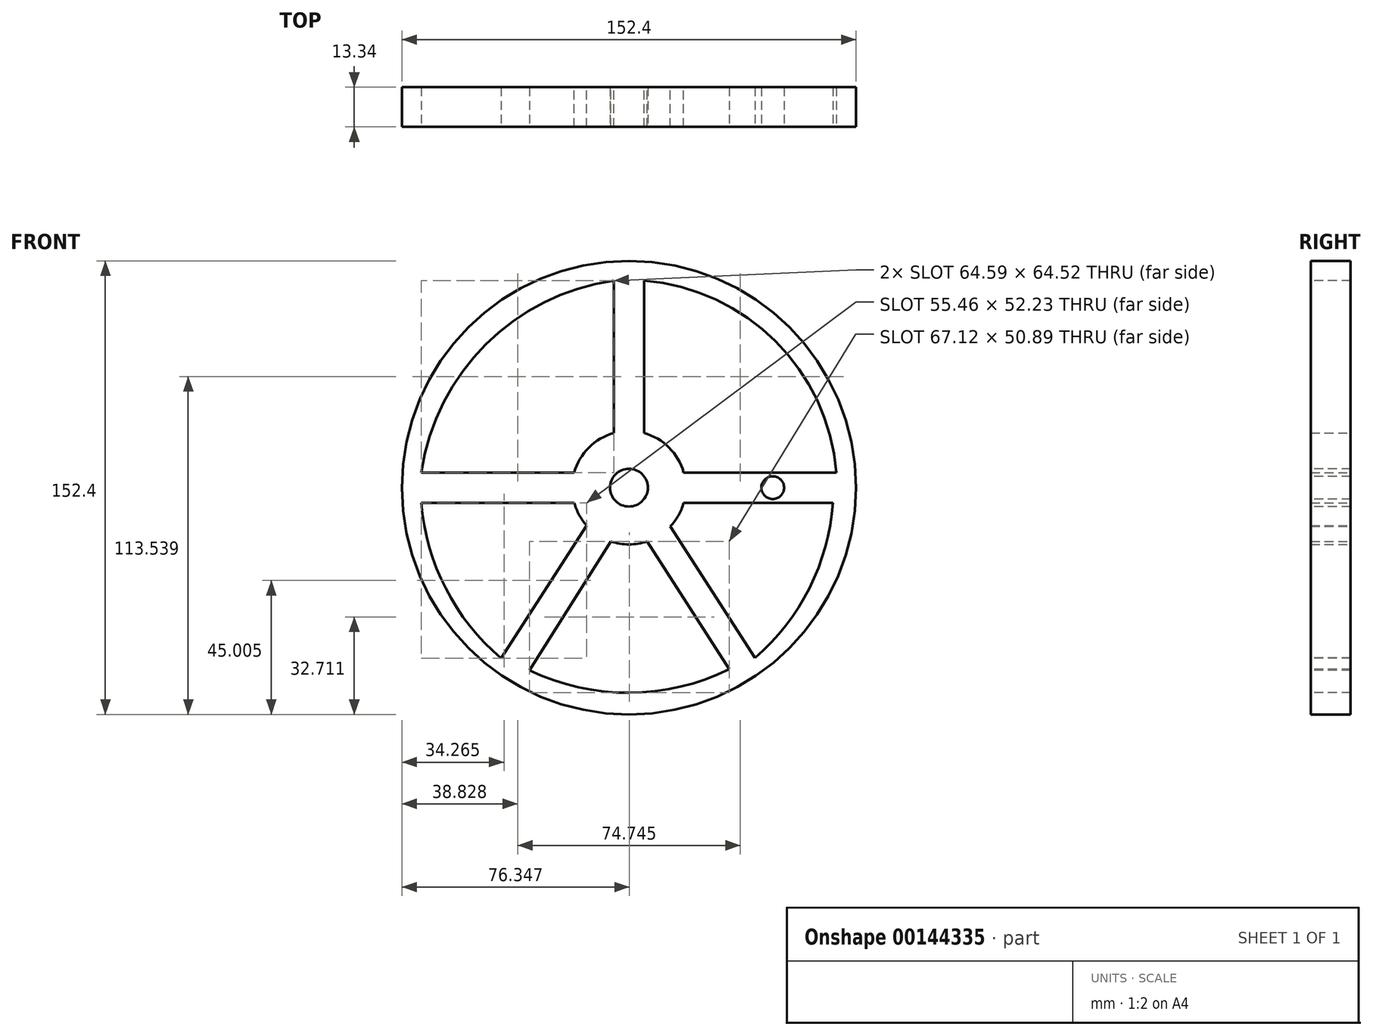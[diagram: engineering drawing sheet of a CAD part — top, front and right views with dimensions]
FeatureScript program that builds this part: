
annotation { "Feature Type Name" : "Feature", "Feature Type Description" : "" }
export const myFeature = defineFeature(function(context is Context, id is Id, definition is map)
    precondition{}
    {
        {
            var Q0;
            Q0=qCreatedBy(makeId("Front.planeOp"),FACE);
            var sketch = newSketch(context, id + "F0", { "sketchPlane" : qUnion([Q0])});
            skCircle(sketch, "E0", {"center": v(0, 0) * mm, "radius": 76.2 * mm});
            skSolve(sketch);
        }
        {
            var Q0;
            Q0 = qSketchRegion(id + "F0", true);
            extrude(context, id + "F1", {"entities" : qUnion([Q0]), "depth" : 13.33 * mm});
        }
        {
            var Q0;
            Q0=makeQuery(id+"F1.opExtrude","CAP_FACE",FACE,{"disambiguationData":[OSD([sQuery(id+"F0.wireOp",EDGE,"E0")])],"isStart":false});
            var sketch = newSketch(context, id + "F2", { "sketchPlane" : qUnion([Q0])});
            skLineSegment(sketch, "E1", {"start": v(-93.5, 0) * mm, "end": v(106.98, 0) * mm, "construction": true});
            skLineSegment(sketch, "E2", {"start": v(0, 114.19) * mm, "end": v(0, -142.49) * mm, "construction": true});
            skCircle(sketch, "E3", {"center": v(0, 0) * mm, "radius": 5.08 * mm, "construction": true});
            skLineSegment(sketch, "E4", {"start": v(51.4, 79.91) * mm, "end": v(-51.4, -79.91) * mm, "construction": true});
            skLineSegment(sketch, "E5", {"start": v(-51.4, 79.91) * mm, "end": v(51.4, -79.91) * mm, "construction": true});
            skArc(sketch, "E6", {"start": v(-5.08, 69.6) * mm, "mid": v(-48.1, 48.08) * mm, "end": v(-69.67, 5.08) * mm});
            skArc(sketch, "E7", {"start": v(69.67, 5.08) * mm, "mid": v(49.2, 49.17) * mm, "end": v(5.08, 69.6) * mm});
            skArc(sketch, "E8", {"start": v(42.32, -57.25) * mm, "mid": v(60.58, -33.77) * mm, "end": v(68.45, -5.08) * mm});
            skArc(sketch, "E9", {"start": v(-33.41, -61.34) * mm, "mid": v(0.2, -68.93) * mm, "end": v(33.7, -60.95) * mm});
            skArc(sketch, "E10", {"start": v(-69.67, -5.08) * mm, "mid": v(-61.51, -33.87) * mm, "end": v(-42.9, -57.31) * mm});
            skLineSegment(sketch, "E11", {"start": v(-5.08, 69.6) * mm, "end": v(-5.08, 5.08) * mm});
            skLineSegment(sketch, "E12", {"start": v(-69.67, 5.08) * mm, "end": v(-5.08, 5.08) * mm});
            skLineSegment(sketch, "E13", {"start": v(5.08, 69.6) * mm, "end": v(5.08, 5.08) * mm});
            skLineSegment(sketch, "E14", {"start": v(5.08, 5.08) * mm, "end": v(69.67, 5.08) * mm});
            skLineSegment(sketch, "E15", {"start": v(-69.67, -5.08) * mm, "end": v(-9.3, -5.08) * mm});
            skLineSegment(sketch, "E16", {"start": v(-42.9, -57.31) * mm, "end": v(-9.3, -5.08) * mm});
            skLineSegment(sketch, "E17", {"start": v(-33.41, -61.34) * mm, "end": v(0, -8.54) * mm});
            skLineSegment(sketch, "E18", {"start": v(0, -8.54) * mm, "end": v(33.7, -60.95) * mm});
            skLineSegment(sketch, "E19", {"start": v(42.32, -57.25) * mm, "end": v(8.76, -5.08) * mm});
            skLineSegment(sketch, "E20", {"start": v(8.76, -5.08) * mm, "end": v(68.45, -5.08) * mm});
            skSolve(sketch);
        }
        {
            var Q0;
            Q0 = qSketchRegion(id + "F2", true);
            extrude(context, id + "F3", {"entities" : qUnion([Q0]), "operationType" : NewBodyOperationType.REMOVE, "endBound" : BoundingType.THROUGH_ALL, "oppositeDirection" : true, "depth" : 25.4 * mm});
        }
        {
            var Q0;
            Q0 = qSketchRegion(id + "F2", true);
            extrude(context, id + "F4", {"entities" : qUnion([Q0]), "operationType" : NewBodyOperationType.REMOVE, "oppositeDirection" : true, "depth" : 25.4 * mm});
        }
        {
            var Q0;
            Q0=qCreatedBy(makeId("Front.planeOp"),FACE);
            var sketch = newSketch(context, id + "F5", { "sketchPlane" : qUnion([Q0])});
            skCircle(sketch, "E21", {"center": v(0, 0) * mm, "radius": 19.05 * mm});
            skCircle(sketch, "E22", {"center": v(0, 0) * mm, "radius": 6.35 * mm});
            skSolve(sketch);
        }
        {
            var Q0;
            Q0 = qSketchRegion(id + "F5", true);
            extrude(context, id + "F6", {"entities" : qUnion([Q0]), "operationType" : NewBodyOperationType.ADD, "depth" : 13.33 * mm});
        }
        {
            var Q0;
            Q0=makeQuery(id+"F6.boolean.opBoolean","MERGE",FACE,{"derivedFrom":[makeQuery(id+"F1.opExtrude","CAP_FACE",FACE,{"disambiguationData":[OSD([sQuery(id+"F0.wireOp",EDGE,"E0")])],"isStart":false}),makeQuery(id+"F6.opExtrude","CAP_FACE",FACE,{"disambiguationData":[OSD([sQuery(id+"F5.wireOp",EDGE,"E21"),sQuery(id+"F5.wireOp",EDGE,"E22")])],"isStart":false})]});
            var sketch = newSketch(context, id + "F7", { "sketchPlane" : qUnion([Q0])});
            skCircle(sketch, "E23.0", {"center": v(0, 0) * mm, "radius": 6.35 * mm});
            skSolve(sketch);
        }
        {
            var Q0;
            Q0 = qSketchRegion(id + "F7", true);
            extrude(context, id + "F8", {"entities" : qUnion([Q0]), "operationType" : NewBodyOperationType.REMOVE, "oppositeDirection" : true, "depth" : 25.4 * mm});
        }
        {
            var Q0;
            Q0=makeQuery(id+"F6.boolean.opBoolean","MERGE",FACE,{"derivedFrom":[makeQuery(id+"F1.opExtrude","CAP_FACE",FACE,{"disambiguationData":[OSD([sQuery(id+"F0.wireOp",EDGE,"E0")])],"isStart":false}),makeQuery(id+"F6.opExtrude","CAP_FACE",FACE,{"disambiguationData":[OSD([sQuery(id+"F5.wireOp",EDGE,"E21"),sQuery(id+"F5.wireOp",EDGE,"E22")])],"isStart":false})]});
            var sketch = newSketch(context, id + "F9", { "sketchPlane" : qUnion([Q0])});
            skCircle(sketch, "E24", {"center": v(48.26, 0) * mm, "radius": 3.81 * mm});
            skSolve(sketch);
        }
        {
            var Q0;
            Q0 = qSketchRegion(id + "F9", true);
            extrude(context, id + "F10", {"entities" : qUnion([Q0]), "operationType" : NewBodyOperationType.REMOVE, "oppositeDirection" : true, "depth" : 25.4 * mm});
        }
    });
